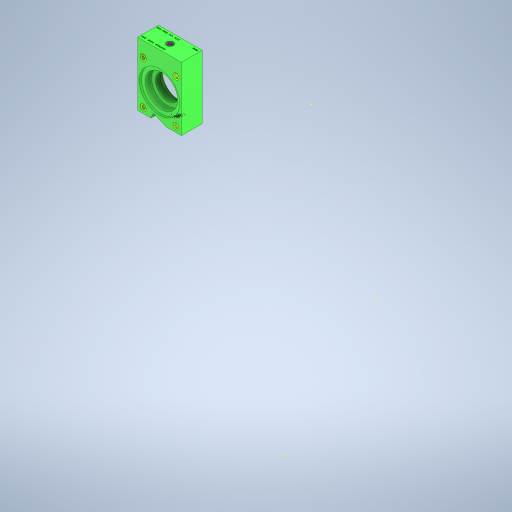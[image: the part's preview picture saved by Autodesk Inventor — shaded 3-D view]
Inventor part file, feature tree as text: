
AUTODESK INVENTOR PART (.ipt)
format: ipt  version: 2024.1 (Build 281209000, 209)  size: 1,149,440 bytes
history: native  units: in
note: dims shown in document units (in); Inventor stores cm internally (conversion verified against a paired STEP export)
features: hole x7, extrude x5, sketch x4, fillet x1
ambient origin geometry x8: Origin, YZ Plane, XZ Plane, XY Plane, X Axis, Y Axis, Z Axis, Center Point
bodies: Solid1 (feature_tree)
feature tree (17):
  extrude  "Extrusion1"  Depth=0.4in TaperAngle=0.0deg
  extrude  "Extrusion2"  Depth=0.0312in
  extrude  "Extrusion3"  Depth=0.0312in
  hole  "Hole1"  [1 undecoded]
  hole  "Hole2"  [1 undecoded]
  extrude  "Extrusion4"  Depth=0.0312in
  hole  "Hole5"  [1 undecoded]
  hole  "Hole6"  [1 undecoded]
  fillet  "Fillet1"  Radius=1.0in
  sketch  "Sketch7"  dims[d13=0.06in d14=0.75in d15=0.507in d16=0.25in d17=0.5635in d18=1.0in d19=0.8108in d20=0.4583in d21=0.29in d22=0.04in d23=0.75in d24=0.507in d25=0.25in d26=0.5635in d27=1.0in d28=0.8108in d29=0.213in d30=0.75in d31=0.507in d32=0.25in d33=0.5635in d34=0.25in d35=0.0in d36=0.75in d38=135.0deg d39=0.4583in d40=112.5deg d41=0.25in d42=1.0in d43=0.0in d44=0.29in d45=0.196in d46=0.211in d47=0.22in d48=0.375in d49=0.25in d50=0.5635in d51=0.22in d52=0.0in d53=0.06in d54=0.75in d55=0.375in d56=0.25in d57=0.5635in d58=0.6in d59=0.8108in d60=0.0312in d61=0.13in d62=1.0in d63=0.375in d64=0.25in d65=0.5635in d66=0.484in d67=0.8108in d68=1.0in d69=0.0in]
  extrude  "Extrusion5"  Depth=0.0312in
  hole  "Hole7"  [1 undecoded]
  hole  "Hole3"  [1 undecoded]
  hole  "Hole4"  [1 undecoded]
  sketch  "Sketch1"  dims[d0=0.5in d1=0.0in d2=0.4in d3=0.0in]
  sketch  "Sketch2"  dims[d4=0.6in d5=0.0in]
  sketch  "Sketch5"  dims[d6=0.211in d7=0.25in d8=0.507in d9=0.25in d10=0.5635in d11=0.25in d12=0.0in]
note: 7 required parameter values undecoded (feature->parameter linkage not recoverable at this tier; creation-order binding heuristic only, values carry confidence <= 0.55)
